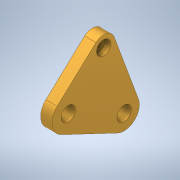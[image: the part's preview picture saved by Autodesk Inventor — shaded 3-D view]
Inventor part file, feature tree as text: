
AUTODESK INVENTOR PART (.ipt)
format: ipt  version: 2020 (Build 240168000, 168)  size: 152,576 bytes
history: native  units: in
note: dims shown in document units (in); Inventor stores cm internally (conversion verified against a paired STEP export)
features: extrude x3, sketch x3, projected_geometry x1
ambient origin geometry x8: Origin, YZ Plane, XZ Plane, XY Plane, X Axis, Y Axis, Z Axis, Center Point
bodies: Solid1 (feature_tree)
feature tree (7):
  extrude  "Extrusion1"  Depth=0.4523in
  extrude  "Extrusion2"  Depth=0.2118in
  extrude  "Extrusion3"  Depth=0.1575in TaperAngle=0.0deg
  sketch  "Sketch1"  dims[d0=0.2008in d1=0.2008in d3=0.4523in]
  sketch  "Sketch2"  dims[d4=0.2118in d5=0.8586in]
  projected_geometry  "Projected Loop1"
  sketch  "Sketch3"  dims[d6=0.8656in d7=0.1575in d8=0.0in d11=0.0787in d12=0.315in d13=0.1575in d14=0.0in d15=0.1969in d16=0.0787in d17=0.0in d20=0.7087in d21=0.4228in]
